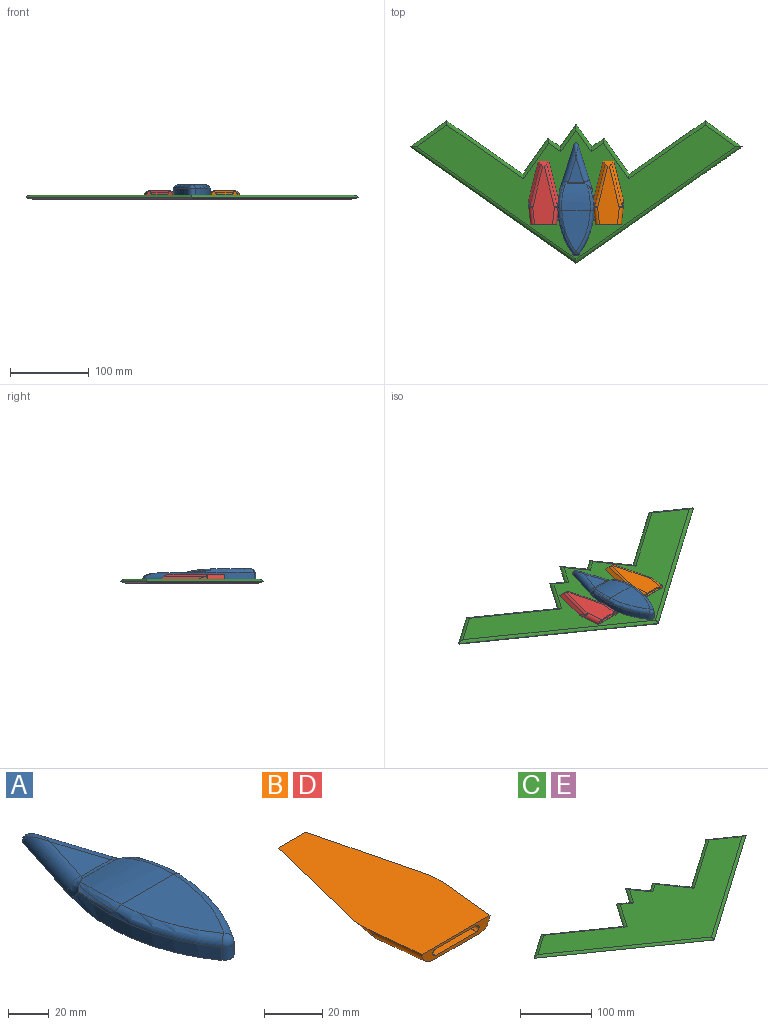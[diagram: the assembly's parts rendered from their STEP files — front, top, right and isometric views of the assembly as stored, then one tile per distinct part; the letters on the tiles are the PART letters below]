
ASSEMBLY  parts=5 mates=4
PART A: 22 faces, bbox 63.3x152.4x14.2 mm
  f0: plane 30.95x19.82mm, normal (0,0,1), area 306.7mm2, adj f14,f18,f19
  f1: plane 3.42x1.1mm, normal (0.95,0.3,0), area 0.5mm2, adj f3,f5,f17
  f2: plane 3.42x1.1mm, normal (-0.95,0.3,0), area 0.5mm2, adj f3,f4,f20
  f3: plane 143.54x46.57mm, normal (0,0,-1), area 4386.9mm2, adj f1,f2,f4,f5,f7,f14,f16,f18
  f4: cylinder r=101.6mm len=90.1mm, axis (0,0,-1), area 702.2mm2, adj f2,f3,f7,f12,f20
  f5: cylinder r=101.6mm len=90.1mm, axis (0,0,-1), area 702.2mm2, adj f1,f3,f7,f10,f17
  f6: plane 52.65x36.25mm, normal (0,0,1), area 1263.8mm2, adj f8,f10,f11,f12
  f7: cylinder r=5.08mm len=8.26mm, axis (0,0,-1), area 75.2mm2, adj f3,f4,f5,f11
  f8: cylinder r=120.8mm len=36.25mm, axis (1,0,0), area 1095.6mm2, adj f6,f9,f13,f17,f19,f20
  f9: bspline ~40.86x10.39mm, area 98.4mm2, adj f8,f10,f15,f17
  f10: torus R=96.69mm, axis (0,0,1), area 493.8mm2, adj f5,f6,f9,f11,f15,f17
  f11: torus R=0.17mm, axis (0,0,1), area 48.3mm2, adj f6,f7,f10,f12
  f12: torus R=96.69mm, axis (0,0,1), area 493.8mm2, adj f4,f6,f11,f13,f20,f21
  f13: bspline ~40.86x10.39mm, area 98.4mm2, adj f8,f12,f20,f21
  f14: cylinder r=7.62mm len=47.98mm, axis (0.3,-0.95,0), area 481.4mm2, adj f0,f3,f16,f17
  f15: bspline ~37.41x12.42mm, area 47mm2, adj f9,f10,f17
  f16: bspline ~24.99x8.72mm, area 47mm2, adj f3,f14,f18
  f17: bspline ~12.65x11.31mm, area 87.8mm2, adj f1,f5,f8,f9,f10,f14,f15,f19
  f18: cylinder r=7.62mm len=47.98mm, axis (0.3,0.95,0), area 481.4mm2, adj f0,f3,f16,f20
  f19: cylinder r=7.62mm len=22.54mm, axis (1,0,0), area 45.5mm2, adj f0,f8,f17,f20
  f20: bspline ~12.65x11.31mm, area 87.8mm2, adj f2,f4,f8,f12,f13,f18,f19,f21
  f21: bspline ~37.58x12.15mm, area 47mm2, adj f12,f13,f20
PART B: 24 faces, bbox 39.8x80.4x8.7 mm
  f0: plane 33.02x5.08mm, normal (0,-1,0), area 96.6mm2, adj f1,f2,f9,f12,f15,f16,f17,f18
  f1: plane 79.87x38.09mm, normal (0,0,1), area 2370.5mm2, adj f0,f3,f4,f5,f9,f11,f12,f14
  f2: plane 72.69x27.45mm, normal (0,0,-1), area 1304.3mm2, adj f0,f6,f7,f8,f9,f12
  f3: plane 57.12x14.39mm, normal (-0.69,0.17,-0.71), area 262.2mm2, adj f1,f4,f6,f14
  f4: plane 13.48x3.59mm, normal (0,0.71,-0.71), area 54.2mm2, adj f1,f3,f5,f7
  f5: plane 57.12x14.39mm, normal (0.69,0.17,-0.71), area 262.2mm2, adj f1,f4,f8,f11
  f6: cylinder r=5.08mm len=54.39mm, axis (-0.24,-0.97,0), area 214.7mm2, adj f2,f3,f7,f13
  f7: cylinder r=5.08mm len=7.86mm, axis (-1,0,0), area 20.8mm2, adj f2,f4,f6,f8
  f8: cylinder r=5.08mm len=54.39mm, axis (-0.24,0.97,0), area 214.7mm2, adj f2,f5,f7,f10
  f9: cylinder r=5.08mm len=22.43mm, axis (0.11,0.99,0), area 172.9mm2, adj f0,f1,f2,f10
  f10: sphere r=5.08mm, area 5.2mm2, adj f8,f9,f11
  f11: cylinder r=5.08mm len=11.85mm, axis (0.1,0.94,0.32), area 25.3mm2, adj f1,f5,f10
  f12: cylinder r=5.08mm len=22.43mm, axis (0.11,-0.99,0), area 172.9mm2, adj f0,f1,f2,f13
  f13: sphere r=5.08mm, area 5.2mm2, adj f6,f12,f14
  f14: cylinder r=5.08mm len=11.85mm, axis (0.1,-0.94,-0.32), area 25.3mm2, adj f1,f3,f13
  f15: cylinder r=1.27mm len=42.16mm, axis (0,-1,0), area 168.2mm2, adj f0,f16,f22,f23
  f16: plane 42.16x0.1mm, normal (1,0,0), area 4.4mm2, adj f0,f15,f17,f23
  f17: plane 42.16x19.99mm, normal (0,0,1), area 842.7mm2, adj f0,f16,f18,f23
  f18: plane 42.16x0.1mm, normal (-1,0,0), area 4.4mm2, adj f0,f17,f19,f23
  f19: cylinder r=1.27mm len=42.16mm, axis (0,-1,0), area 168.2mm2, adj f0,f18,f20,f23
  f20: plane 42.16x0.1mm, normal (-1,0,0), area 4.4mm2, adj f0,f19,f21,f23
  f21: plane 42.16x19.99mm, normal (0,0,-1), area 842.7mm2, adj f0,f20,f22,f23
  f22: plane 42.16x0.1mm, normal (1,0,0), area 4.4mm2, adj f0,f15,f21,f23
  f23: plane 22.53x2.75mm, normal (0,-1,0), area 60mm2, adj f15,f16,f17,f18,f19,f20,f21,f22
PART C: 14 faces, bbox 421.3x180.3x2.5 mm
  f0: plane 405.99x169.55mm, normal (0,0,1), area 27748.8mm2, adj f2,f3,f4,f5,f6,f7,f8,f9
  f1: plane 421.33x180.29mm, normal (0,0,-1), area 32428.8mm2, adj f2,f3,f4,f5,f6,f7,f8,f9
  f2: cylinder r=5.08mm len=51.64mm, axis (-0.57,0.82,0), area 295.6mm2, adj f0,f1,f3,f4
  f3: cylinder r=5.08mm len=102.36mm, axis (-0.82,-0.57,0), area 628.1mm2, adj f0,f1,f2,f5
  f4: cylinder r=5.08mm len=21.73mm, axis (-0.82,-0.57,0), area 101.3mm2, adj f0,f1,f2,f6
  f5: cylinder r=5.08mm len=49.34mm, axis (-0.82,0.57,0), area 281.7mm2, adj f0,f1,f3,f7
  f6: cylinder r=5.08mm len=34.9mm, axis (0.57,-0.82,0), area 182.4mm2, adj f0,f1,f4,f8
  f7: cylinder r=5.08mm len=213.19mm, axis (0.82,0.57,0), area 1345.8mm2, adj f0,f1,f5,f9
  f8: cylinder r=5.08mm len=34.9mm, axis (0.57,0.82,0), area 182.4mm2, adj f0,f1,f6,f10
  f9: cylinder r=5.08mm len=213.19mm, axis (-0.82,0.57,0), area 1345.8mm2, adj f0,f1,f7,f11
  f10: cylinder r=5.08mm len=21.73mm, axis (0.82,-0.57,0), area 101.3mm2, adj f0,f1,f8,f12
  f11: cylinder r=5.08mm len=49.34mm, axis (0.82,0.57,0), area 281.7mm2, adj f0,f1,f9,f13
  f12: cylinder r=5.08mm len=51.64mm, axis (0.57,0.82,0), area 295.6mm2, adj f0,f1,f10,f13
  f13: cylinder r=5.08mm len=102.36mm, axis (0.82,-0.57,0), area 628.1mm2, adj f0,f1,f11,f12
PART D: same geometry as B
PART E: same geometry as C
PLACE A t=(27.76,-30.48,55.7)mm
PLACE B rot(axis=(0,1,0),180deg) t=(65.24,-62.86,60.78)mm
PLACE C t=(27.76,-112.04,53.16)mm
PLACE D rot(axis=(0,1,0),180deg) t=(-17.04,-62.86,60.78)mm
PLACE E rot(axis=(0,1,0),180deg) t=(27.76,-112.04,53.16)mm
MATE fastened B.f1 <-> C.f0  axis (0,0,-1) through (68.9,-28.12,55.7)mm
MATE fastened D.f1 <-> C.f0  axis (0,0,-1) through (-13.38,-28.12,55.7)mm
MATE fastened E.f1 <-> C.f1  axis (0,0,1) through (27.76,-112.04,53.16)mm
MATE fastened A.f3 <-> C.f0  axis (0,0,-1) through (27.76,-36.68,55.7)mm
